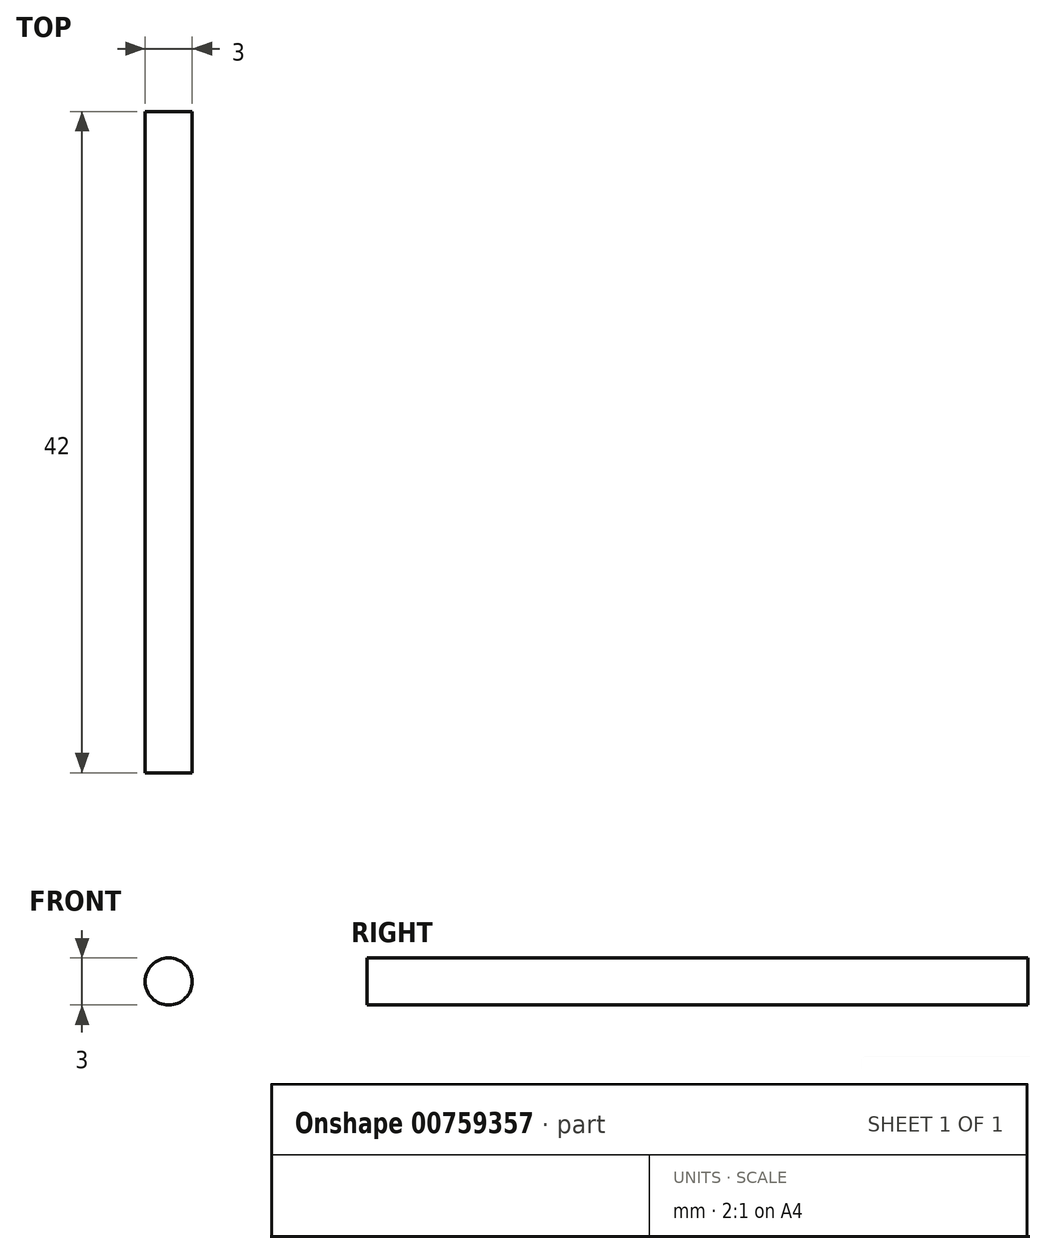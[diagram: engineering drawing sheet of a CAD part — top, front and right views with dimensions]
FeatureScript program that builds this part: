
annotation { "Feature Type Name" : "Feature", "Feature Type Description" : "" }
export const myFeature = defineFeature(function(context is Context, id is Id, definition is map)
    precondition{}
    {
        {
            var Q0;
            Q0=qCreatedBy(makeId("Front.planeOp"),FACE);
            var sketch = newSketch(context, id + "F0", { "sketchPlane" : qUnion([Q0])});
            skCircle(sketch, "E0", {"center": v(0, 0) * mm, "radius": 1.5 * mm});
            skSolve(sketch);
        }
        {
            var Q0;
            Q0=makeQuery(id+"F0.imprint","IMPRINT",FACE,{"disambiguationData":[TD([[makeQuery(id+"F0.imprint","IMPRINT",EDGE,{"derivedFrom":sQuery(id+"F0.wireOp",EDGE,"E0")}),1.0]])]});
            extrude(context, id + "F1", {"entities" : qUnion([Q0]), "depth" : 42 * mm, "offsetDistance" : 25 * mm});
        }
    });
